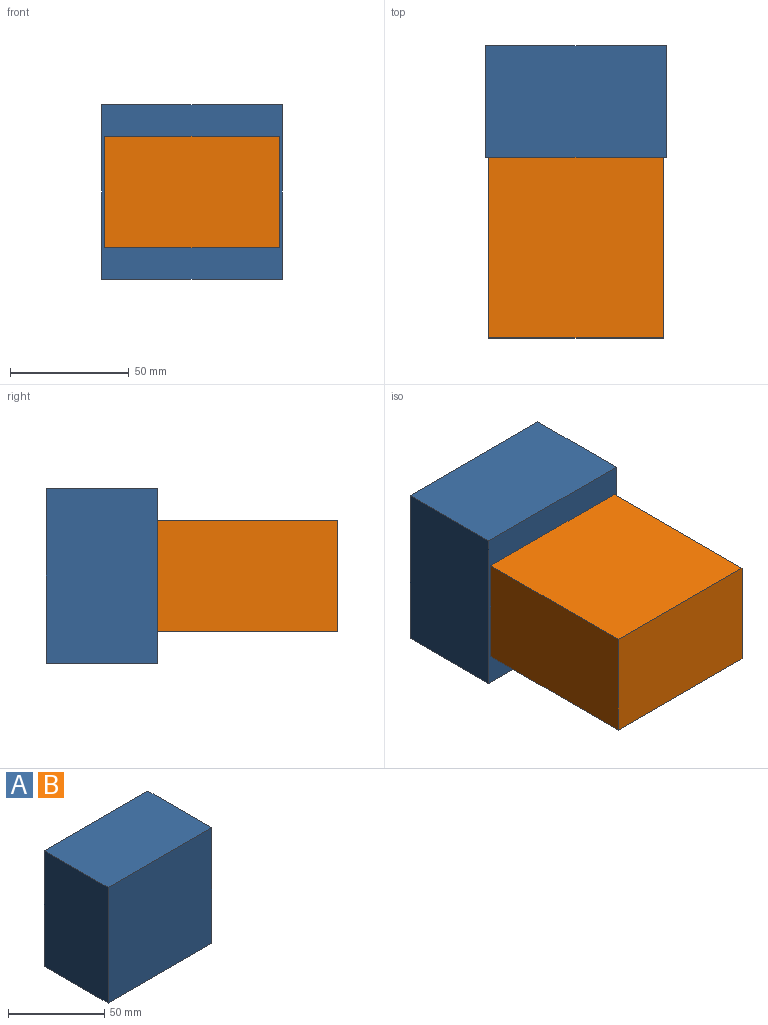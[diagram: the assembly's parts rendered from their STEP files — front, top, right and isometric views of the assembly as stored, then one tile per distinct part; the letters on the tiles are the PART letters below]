
ASSEMBLY  parts=2 mates=1
PART A: 6 faces, bbox 76x46.7x73.4 mm
  f0: plane 75.96x73.41mm, normal (0,1,0), area 5575.7mm2, adj f1,f3,f4,f5
  f1: plane 73.41x46.68mm, normal (-1,0,0), area 3426.3mm2, adj f0,f2,f4,f5
  f2: plane 75.96x73.41mm, normal (0,-1,0), area 5575.7mm2, adj f1,f3,f4,f5
  f3: plane 73.41x46.68mm, normal (1,0,0), area 3426.3mm2, adj f0,f2,f4,f5
  f4: plane 75.96x46.68mm, normal (0,0,1), area 3545.4mm2, adj f0,f1,f2,f3
  f5: plane 75.96x46.68mm, normal (0,0,-1), area 3545.4mm2, adj f0,f1,f2,f3
PART B: same geometry as A
PLACE A t=(25.79,2.26,13.28)mm
PLACE B rot(axis=(-0.58,-0.58,0.58),120deg) t=(-25.69,24.16,45.02)mm
MATE fastened B.f3 <-> A.f2  axis (0,1,0) through (-62.39,-26.04,49.98)mm
